# Revit family: 65092203
name_source: partatom
category: Plumbing Fixtures
revit_build: Autodesk Revit 2016 (Build: 20150714_1515(x64)
units: mm (PartAtom-declared; Revit-internal decimal feet)

## family parameters
Always vertical = Yes
Cut with Voids When Loaded = No
OmniClass Number = 23.45.55.00
OmniClass Title = Sanitary Faucets, Wastes
Part Type = Normal
Room Calculation Point = No
Round Connector Dimension = Use Diameter
Shared = No
Work Plane-Based = No

## types (1)
- 65092203 Washbasin faucet
    2D/3D/BIM Files URL = http://static.hansa.com
    Advanced Features = ECO button
    Aerator = HONEYCOMB;CACHE integrated aerator
    Approval ABP = P-IX 28781/IO
    AssetType = Fixed
    BIMObjectName = 65092203
    BodyMaterial = Brass
    Brand = Hansa
    Catalog Drawing URL = http://static.hansa.com
    Category = Bathroom
    Class = Single lever
    CloseOffRating = 0
    Color = Chrome
    Connection Size = G3/8
    ConvergoRefNr = 0087-1806-0139-FI
    Customs Code = 84818011
    DN Size = DN15
    Dimension Drawing URL = http://static.hansa.com
    DurationUnit = Year
    EAN Number = 4015474273436
    Extensions = Rapid pop-up waste
    FDV Document URL = http://www.hansa.com
    FaucetMainMaterial = Brass
    Features = Single lever
    Finish = Polished
    Flow = EcoFlow control
    Flow Drawing URL = http://static.hansa.com
    Flow Rate At 300kPa = 0.1 L/s
    FlowCoefficient = 0
    Group = Washbasin faucet
    IfcExportAs = IfcValveType
    IfcExportType = FAUCET
    InletConnectionSize = 10 mm  [stored 0.0328084 ft]
    Installation Type = Deck mounted
    Installation and Maintenance = http://static.hansa.com
    Lever Handle = Easy-grip lever
    ManufacterURL = http://www.hansa.com
    Manufacturer = Hansa
    ManufacturerName = Hansa
    Market = AUT;BEL;CZE;DEU;ESP;FRA;INT;ITA;NLD;SVK
    Material = Brass
    Max. Hot Water Supply = 80 °C
    Mechanical Parts = Litter filter
    Model = 65092203 Washbasin faucet
    ModelReference = 65092203
    Mounting Holes = 1 mounting hole
    NBSDescription = Water supply fittings for wash basins and troughs
    NBSReference = 45-35-70/371
    Name = 65092203 Washbasin faucet
    Name_en = 65092203 Washbasin faucet
    Noise Class = I (ISO 3822)
    NominalDepth = 145 mm  [stored 0.475722 ft]
    NominalHeight = 163 mm  [stored 0.534777 ft]
    NominalWidth = 54 mm  [stored 0.177165 ft]
    Package Weight = 1.61 kg
    Package external Dimensions = 520 x 215 x 70
    Pipes = Flexible inlet pipes
    Pressure Loss With Flow 01ls = 90000.0 Pa
    Product Code = 65092203
    Product Datasheet = http://www.hansa.com
    Product Family = HANSAFIT
    Product Image URL = http://static.hansa.com
    Product URL = http://static.hansa.com
    Projection = 98 mm
    Revision = 2
    STF Certificate = VTT-RTH-00007-14
    Shape = Sculptured
    Size = 54x145x163 mm
    Spare Parts = http://static.hansa.com
    Spout Type = Fixed spout
    URL ABP = http://static.hansa.com
    URL STF = http://static.hansa.com
    Uniclass2 = Pr_40_30_96_96
    Uniclass2015Description = Washbasin manual water supply sets
    Uniclass2015Reference = Pr_40_20_87_96
    Version = 2
    VersionDate = 01/01/2019
    WarrantyDescription = http://warranty.hansa.com
    WarrantyDurationUnit = Year
    WorkingPressure = 50 - 1000 kPa

note: [stored X ft] marks values corroborated as IEEE doubles in the binary element streams (Revit-internal decimal feet)

## geometry (parser evidence)
native form markers: Sweep x5
no freeform markers — native parametric forms only
